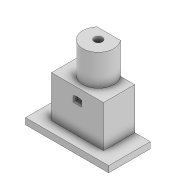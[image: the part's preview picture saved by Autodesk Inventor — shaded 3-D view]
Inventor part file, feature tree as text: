
AUTODESK INVENTOR PART (.ipt)
format: ipt  version: 2022 (Build 260153000, 153)  size: 178,688 bytes
history: native  units: mm
features: extrude x9, sketch x9, projected_geometry x2
ambient origin geometry x8: Origin, YZ Plane, XZ Plane, XY Plane, X Axis, Y Axis, Z Axis, Center Point
bodies: Solid1 (feature_tree)
feature tree (20):
  extrude  "Extrusion1"  Depth=25.0mm
  extrude  "Extrusion2"  Depth=20.0mm TaperAngle=0.0deg
  extrude  "Extrusion3"  Depth=100.0mm TaperAngle=0.0deg
  extrude  "Extrusion4"  Depth=15.0mm TaperAngle=0.0deg
  extrude  "Extrusion6"  Depth=40.0mm
  extrude  "Extrusion8"  Depth=10.0mm TaperAngle=0.0deg
  extrude  "Extrusion9"  Depth=2.0mm
  extrude  "Extrusion10"  Depth=3.0mm
  extrude  "Extrusion11"  Depth=15.0mm
  sketch  "Sketch1"  dims[d0=12.2mm d1=25.0mm]
  sketch  "Sketch2"  dims[d2=20.0mm d3=20.0mm d4=0.0mm]
  sketch  "Sketch3"  dims[d5=3.9mm d6=100.0mm d7=0.0mm]
  projected_geometry  "Projected Loop1"
  sketch  "Sketch4"  dims[d8=15.0mm d9=15.0mm d10=0.0mm]
  sketch  "Sketch6"  dims[d11=30.0mm d12=40.0mm]
  sketch  "Sketch8"  dims[d13=3.0mm d14=0.0mm d21=10.0mm d22=0.0mm]
  sketch  "Sketch9"  dims[d26=100.0mm d27=0.0mm d28=2.0mm]
  projected_geometry  "Projected Loop3"
  sketch  "Sketch10"  dims[d29=2.0mm d30=3.0mm]
  sketch  "Sketch11"  dims[d31=2.0mm d32=0.0mm d33=9.8mm d34=15.0mm d35=0.0mm d36=100.0mm d37=0.0mm]
